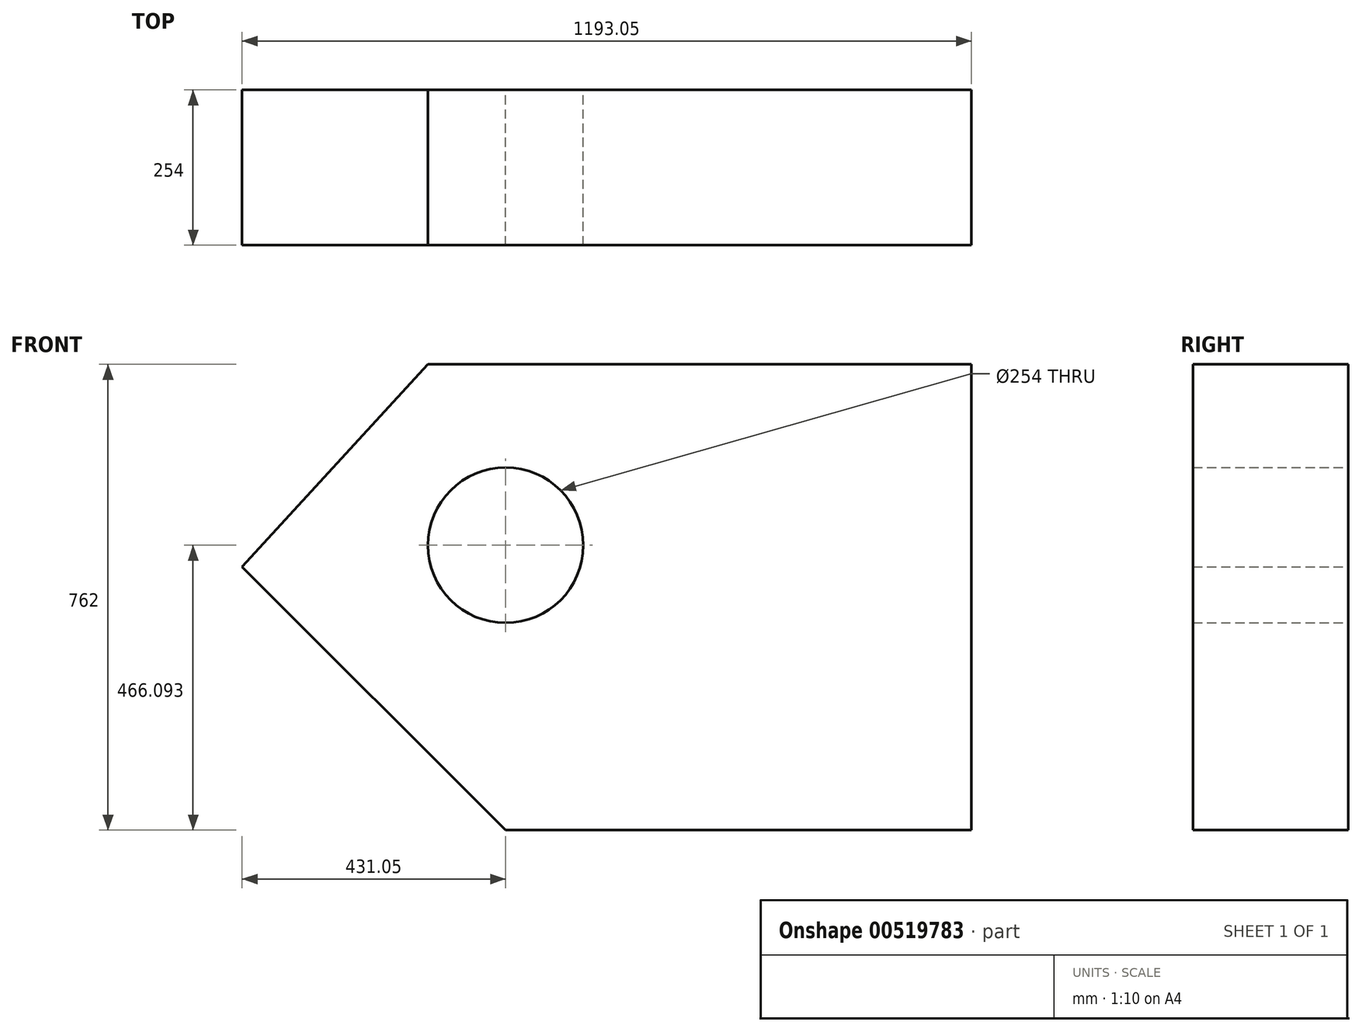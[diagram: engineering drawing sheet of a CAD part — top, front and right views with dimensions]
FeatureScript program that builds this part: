
annotation { "Feature Type Name" : "Feature", "Feature Type Description" : "" }
export const myFeature = defineFeature(function(context is Context, id is Id, definition is map)
    precondition{}
    {
        {
            var Q0;
            Q0=qCreatedBy(makeId("Front.planeOp"),FACE);
            var sketch = newSketch(context, id + "F0", { "sketchPlane" : qUnion([Q0])});
            skLineSegment(sketch, "E0", {"start": v(0, 0) * mm, "end": v(762, 0) * mm});
            skLineSegment(sketch, "E1", {"start": v(0, 0) * mm, "end": v(-431.05, 431.05) * mm});
            skLineSegment(sketch, "E2", {"start": v(762, 0) * mm, "end": v(762, 762) * mm});
            skLineSegment(sketch, "E3", {"start": v(762, 762) * mm, "end": v(-127, 762) * mm});
            skLineSegment(sketch, "E4", {"start": v(-127, 762) * mm, "end": v(-431.05, 431.05) * mm});
            skCircle(sketch, "E5", {"center": v(0, 466.1) * mm, "radius": 127 * mm});
            skSolve(sketch);
        }
        {
            var Q0;
            Q0 = qSketchRegion(id + "F0", true);
            extrude(context, id + "F1", {"entities" : qUnion([Q0]), "depth" : 254 * mm, "offsetDistance" : 25.4 * mm});
        }
    });
